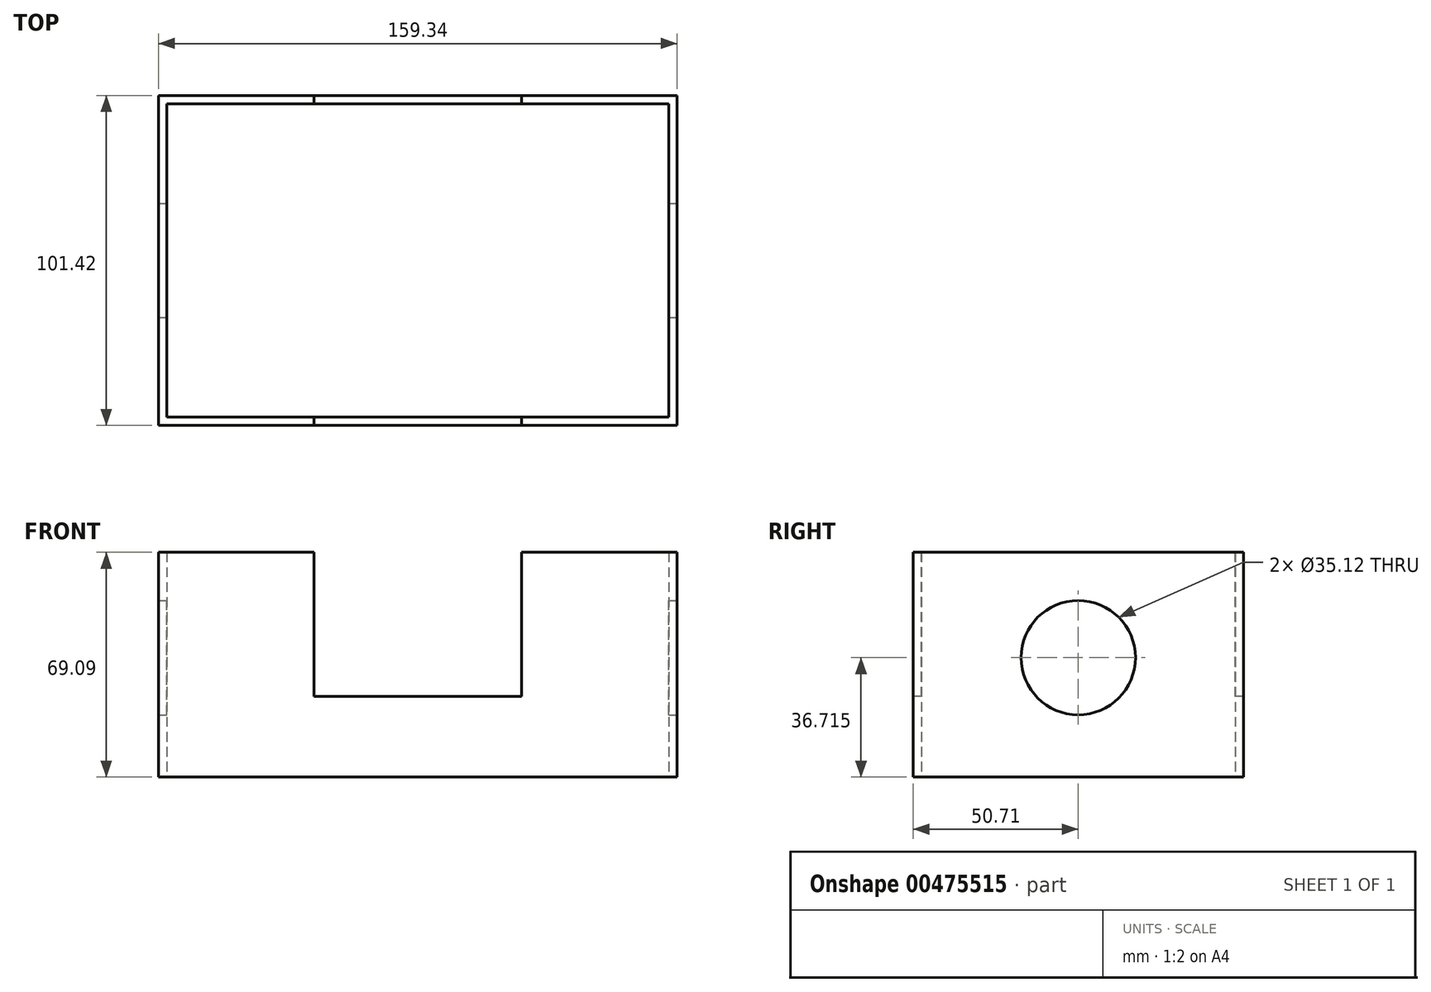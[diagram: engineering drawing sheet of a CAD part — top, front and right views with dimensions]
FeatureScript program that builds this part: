
annotation { "Feature Type Name" : "Feature", "Feature Type Description" : "" }
export const myFeature = defineFeature(function(context is Context, id is Id, definition is map)
    precondition{}
    {
        {
            var Q0;
            Q0=qCreatedBy(makeId("Top.planeOp"),FACE);
            var sketch = newSketch(context, id + "F0", { "sketchPlane" : qUnion([Q0])});
            skLineSegment(sketch, "E0.bottom", {"start": v(79.67, 50.71) * mm, "end": v(-79.67, 50.71) * mm});
            skLineSegment(sketch, "E0.top", {"start": v(79.67, -50.71) * mm, "end": v(-79.67, -50.71) * mm});
            skLineSegment(sketch, "E0.left", {"start": v(79.67, 50.71) * mm, "end": v(79.67, -50.71) * mm});
            skLineSegment(sketch, "E0.right", {"start": v(-79.67, 50.71) * mm, "end": v(-79.67, -50.71) * mm});
            skPoint(sketch, "E0.middle", {"position": v(0, 0) * mm});
            skSolve(sketch);
        }
        {
            var Q0;
            Q0 = qSketchRegion(id + "F0", true);
            extrude(context, id + "F1", {"entities" : qUnion([Q0]), "depth" : 69.1 * mm});
        }
        {
            var Q0;
            Q0=makeQuery(id+"F1.opExtrude","CAP_FACE",FACE,{"disambiguationData":[OSD([sQuery(id+"F0.wireOp",EDGE,"E0.bottom"),sQuery(id+"F0.wireOp",EDGE,"E0.top"),sQuery(id+"F0.wireOp",EDGE,"E0.left"),sQuery(id+"F0.wireOp",EDGE,"E0.right")])],"isStart":false});
            var Q1;
            Q1=makeQuery(id+"F1.opExtrude","CAP_FACE",FACE,{"disambiguationData":[OSD([sQuery(id+"F0.wireOp",EDGE,"E0.bottom"),sQuery(id+"F0.wireOp",EDGE,"E0.top"),sQuery(id+"F0.wireOp",EDGE,"E0.left"),sQuery(id+"F0.wireOp",EDGE,"E0.right")])],"isStart":true});
            shell(context, id + "F2", {"entities" : qUnion([Q0, Q1]), "thickness" : 2.54 * mm});
        }
        {
            var Q0;
            Q0=makeQuery(id+"F1.opExtrude","SWEPT_FACE",FACE,{"disambiguationData":[OSD([sQuery(id+"F0.wireOp",EDGE,"E0.top")])]});
            var sketch = newSketch(context, id + "F3", { "sketchPlane" : qUnion([Q0])});
            skLineSegment(sketch, "E1.bottom", {"start": v(31.85, 24.78) * mm, "end": v(-31.85, 24.78) * mm});
            skLineSegment(sketch, "E1.top", {"start": v(31.85, 113.4) * mm, "end": v(-31.85, 113.4) * mm});
            skLineSegment(sketch, "E1.left", {"start": v(31.85, 24.78) * mm, "end": v(31.85, 113.4) * mm});
            skLineSegment(sketch, "E1.right", {"start": v(-31.85, 24.78) * mm, "end": v(-31.85, 113.4) * mm});
            skPoint(sketch, "E1.middle", {"position": v(0, 69.09) * mm});
            skSolve(sketch);
        }
        {
            var Q0;
            Q0 = qSketchRegion(id + "F3", true);
            extrude(context, id + "F4", {"entities" : qUnion([Q0]), "operationType" : NewBodyOperationType.REMOVE, "endBound" : BoundingType.THROUGH_ALL, "oppositeDirection" : true, "depth" : 25.4 * mm});
        }
        {
            var Q0;
            Q0=makeQuery(id+"F1.opExtrude","SWEPT_FACE",FACE,{"disambiguationData":[OSD([sQuery(id+"F0.wireOp",EDGE,"E0.left")])]});
            var sketch = newSketch(context, id + "F5", { "sketchPlane" : qUnion([Q0])});
            skCircle(sketch, "E2", {"center": v(0, 36.72) * mm, "radius": 17.56 * mm});
            skSolve(sketch);
        }
        {
            var Q0;
            Q0 = qSketchRegion(id + "F5", true);
            extrude(context, id + "F6", {"entities" : qUnion([Q0]), "operationType" : NewBodyOperationType.REMOVE, "endBound" : BoundingType.THROUGH_ALL, "oppositeDirection" : true, "depth" : 25.4 * mm});
        }
    });
